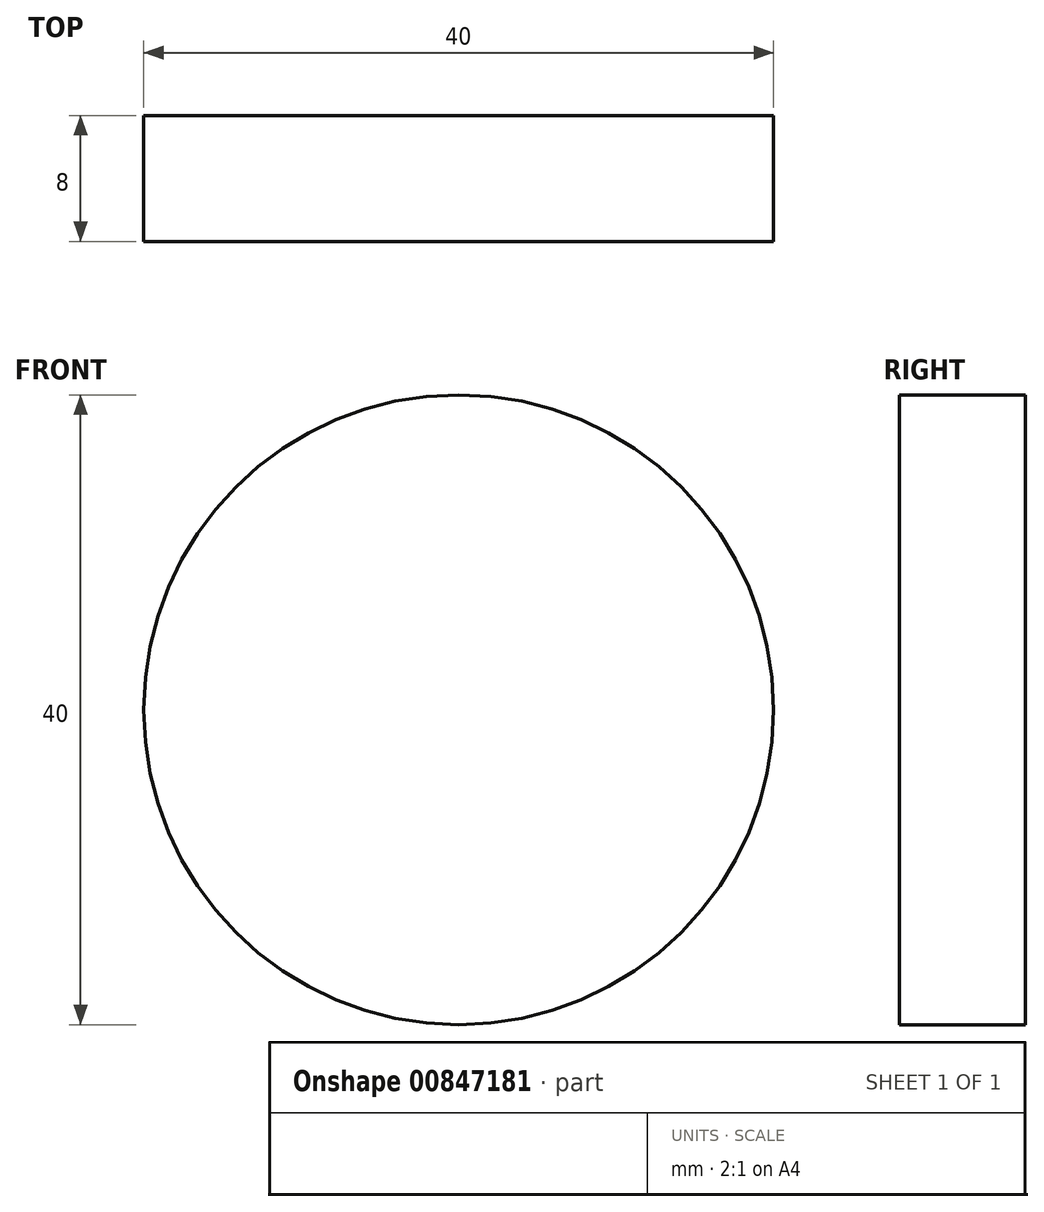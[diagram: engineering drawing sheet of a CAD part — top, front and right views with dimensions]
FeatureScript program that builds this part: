
annotation { "Feature Type Name" : "Feature", "Feature Type Description" : "" }
export const myFeature = defineFeature(function(context is Context, id is Id, definition is map)
    precondition{}
    {
        {
            var Q0;
            Q0=qCreatedBy(makeId("Front.planeOp"),FACE);
            var sketch = newSketch(context, id + "F0", { "sketchPlane" : qUnion([Q0])});
            skCircle(sketch, "E0", {"center": v(0, -1.79) * mm, "radius": 20 * mm});
            skSolve(sketch);
        }
        {
            var Q0;
            Q0 = qSketchRegion(id + "F0", true);
            extrude(context, id + "F1", {"entities" : qUnion([Q0]), "depth" : 8 * mm, "offsetDistance" : 25 * mm});
        }
    });
